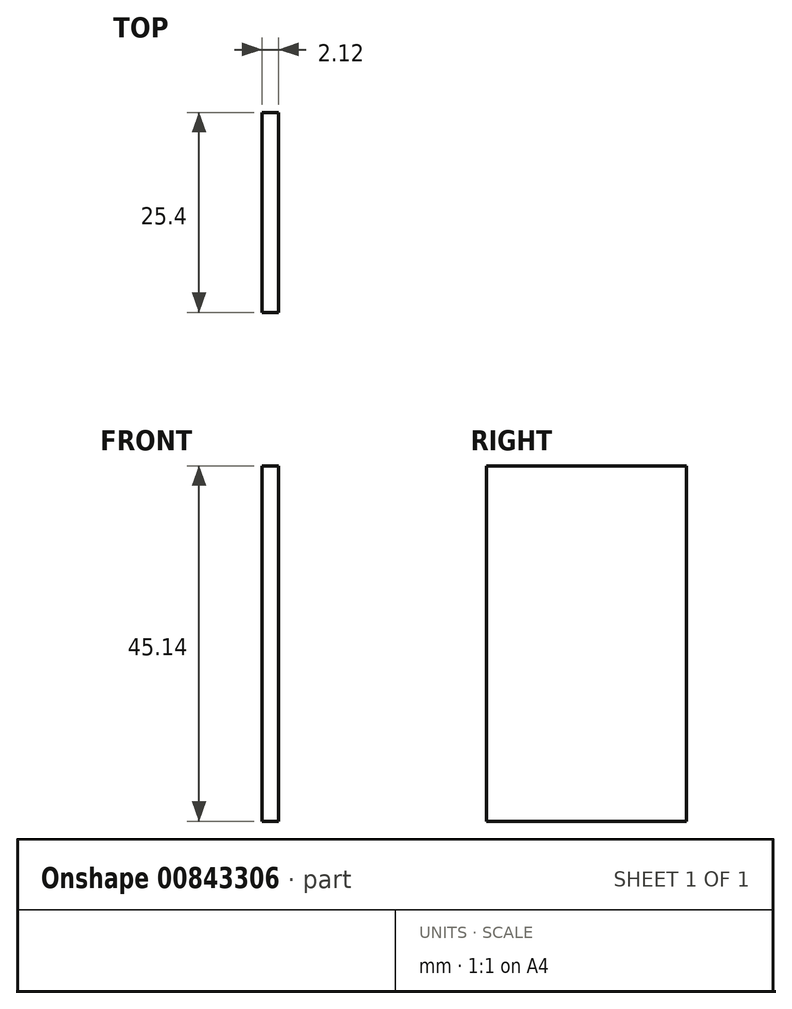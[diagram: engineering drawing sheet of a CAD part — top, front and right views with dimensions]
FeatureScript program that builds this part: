
annotation { "Feature Type Name" : "Feature", "Feature Type Description" : "" }
export const myFeature = defineFeature(function(context is Context, id is Id, definition is map)
    precondition{}
    {
        {
            var Q0;
            Q0=qCreatedBy(makeId("Front.planeOp"),FACE);
            var sketch = newSketch(context, id + "F0", { "sketchPlane" : qUnion([Q0])});
            skLineSegment(sketch, "E0.bottom", {"start": v(-148.77, 61.83) * mm, "end": v(-150.89, 61.83) * mm});
            skLineSegment(sketch, "E0.top", {"start": v(-148.77, 16.7) * mm, "end": v(-150.89, 16.7) * mm});
            skLineSegment(sketch, "E0.left", {"start": v(-148.77, 61.83) * mm, "end": v(-148.77, 16.7) * mm});
            skLineSegment(sketch, "E0.right", {"start": v(-150.89, 61.83) * mm, "end": v(-150.89, 16.7) * mm});
            skSolve(sketch);
        }
        {
            var Q0;
            Q0 = qSketchRegion(id + "F0", true);
            extrude(context, id + "F1", {"entities" : qUnion([Q0]), "depth" : 25.4 * mm, "offsetDistance" : 25.4 * mm});
        }
    });
